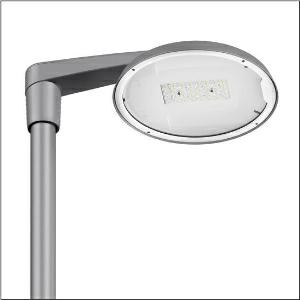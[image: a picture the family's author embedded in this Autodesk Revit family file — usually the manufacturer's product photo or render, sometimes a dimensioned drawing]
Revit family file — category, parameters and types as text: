
# Revit family: dl_50_iq_mini___st0_5a_5xa248b41f08ke_a4ca
name_source: partatom
category: Lighting Fixtures
units: mm (PartAtom-declared; Revit-internal decimal feet)

## family parameters
Cut with Voids When Loaded = No
Host = Face
Light Source = No
Part Type = Normal
Room Calculation Point = No
Round Connector Dimension = Use Diameter
Shared = No

## types (1)
- --- (1 x LED, 5510 lm, 30.8 W, 4000K)
    Apparent Load = 31 VA
    CIE Flux Codes = 43 76 97 100 100
    Color Rendering = 70
    Color Temperature = 4000K
    Default Elevation = 1800 mm
    Description = DL 50 iQ mini, mast luminaire, primary light control with lens, of PMMA, primary optical cover: cover, of toughened safety glass, transparent, light distribution: ST0.5a, light emission: direct distribution, primary light characteristic: asymmetric, installation type: side-entry, post-top, LED, High Power LED, rated luminous flux: 5.510lm, luminous efficacy: 179lm/W, light colour: 740, colour temperature: 4000K, control gear: iQ Street-Remote, control: optimised constant luminous flux control (CLO 2.0), Desk-Remote (wireless, voltage-free reading and setting of iQ features in the workshop via application-optimized NFC function/RFID function), Light-Fading, Smart-Wire, Night-Set, Lumen-Switch, Temp-Guard, Auto-Match, Street-Remote, mains connection: 230..240V, AC, 50/60Hz, connection cable pre-assembled, cable length: 6,5m, start of lifetime: 31W, end of service life: 32W, reduction: 15W, luminaire housing, of diecast aluminium, powder-coated, SITECO metallic grey (DB 702S), inclination adjustable: 0°, 5°, 10° (post-top) | 0°, -5°, -10°, -15° (side-entry), please order mast post-top element or mast side-entry element separately, diameter: 500mm, height: 115mm, post-top: for spigot size d x l = 76 x 100mm; with reducer (optional accessory) 60 x 100mm | side-entry: for spigot size d x l = 60 x 100mm; with reducer (optional accessory) 42 x 100mm, mounting height: 4..6m, protection rating (complete): IP66, insulation class (complete): insulation class II (safety insulation), certification: CE, ENEC, ENEC+, VDE, impact resistance: IK08, permissible operating ambient temperature for outdoor applications: -25..+40°C, standard-compliant lighting for roads and squares, packaging unit: 1 piece

Light Distribution: ST0.5a
    Height = 115 mm
    Lamp = 1 x LED
    Lamp Light Flux = 5510 lm
    Lamp Power = 30.8 W
    Lamp count = 1
    Length = 500 mm
    Luminous efficacy = 179 lm/W
    Manufacturer = Siteco
    ModVariant = No
    Model = 5XA248B41F08KE
    Mounting Place = Pole
    Mounting Type = Pole top
    Number of Poles = 1
    OnlyDefault = Yes
    Power Factor = 1
    Product Name = DL 50 iQ mini | ST0.5a
    Product group = mast luminaire | pylon top
    ProductGroupID = 6100
    Protection Class = Protection class II
    Protection Degree = IP 66
    RLX_Detail_Level = 1
    RLX_Emergency_Light_Flux = 0 lm
    RLX_Emergency_Type = 0
    RLX_Emergency_Type_DB = No
    RlxData = <blob elided: 126773 chars, md5=5c99f083>
    Socket = socket
    Standby Power = 0 W
    System Light Flux = 5510 lm
    System Power = 31 W
    Type Comments = factory setting: luminous flux: 100 % | dim-lin: 254 | 329 mA
    Type Image = l_1251794.jpg
    URL = http://relux.com
    VarID = @adj_144009
    Voltage = 0 V
    Weight = 0.00 kg
    Width = 0 mm  [stored 0 ft]

note: [stored X ft] marks values corroborated as IEEE doubles in the binary element streams (Revit-internal decimal feet)

## geometry (parser evidence)
native form markers: Blend x4, Sweep x12
no freeform markers — native parametric forms only
